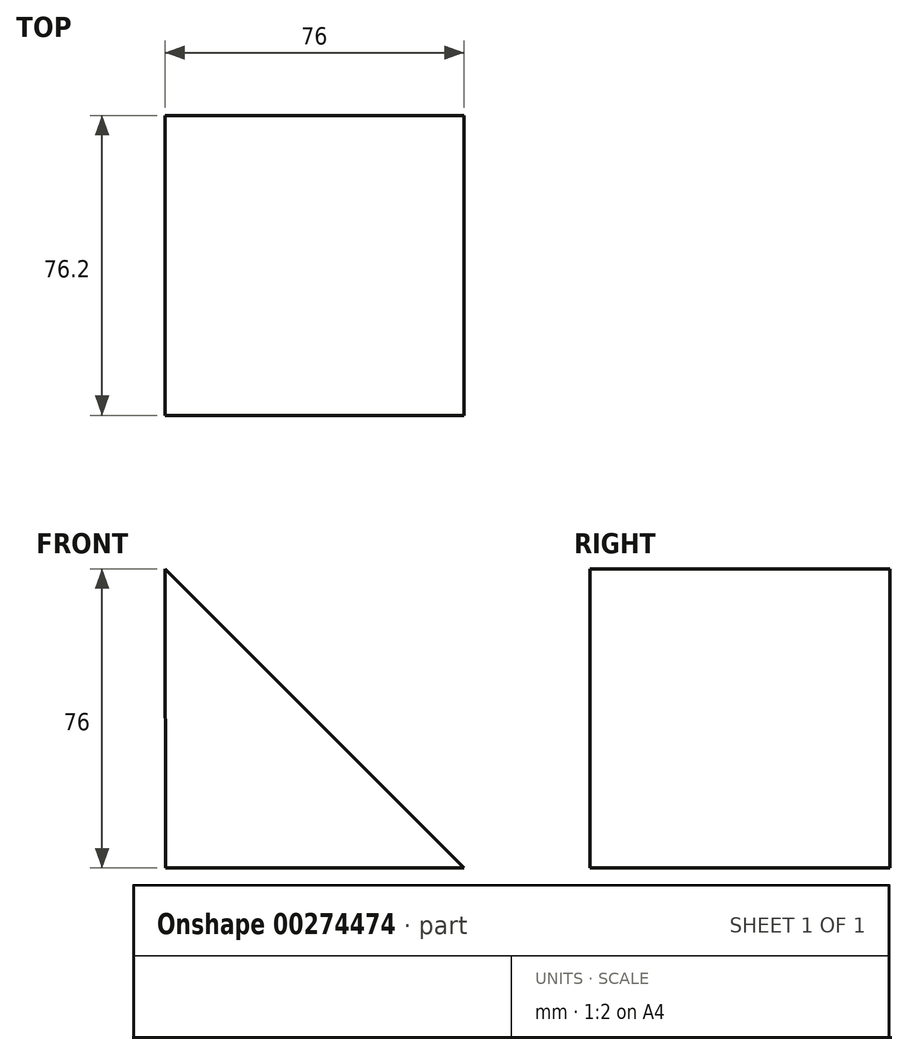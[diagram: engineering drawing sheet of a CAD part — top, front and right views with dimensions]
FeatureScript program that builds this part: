
annotation { "Feature Type Name" : "Feature", "Feature Type Description" : "" }
export const myFeature = defineFeature(function(context is Context, id is Id, definition is map)
    precondition{}
    {
        {
            var Q0;
            Q0=qCreatedBy(makeId("Front.planeOp"),FACE);
            var sketch = newSketch(context, id + "F0", { "sketchPlane" : qUnion([Q0])});
            skLineSegment(sketch, "E0", {"start": v(-76, 76) * mm, "end": v(0, 0) * mm});
            skLineSegment(sketch, "E1", {"start": v(0, 0) * mm, "end": v(-75.8, 0) * mm});
            skLineSegment(sketch, "E2", {"start": v(-75.8, 0) * mm, "end": v(-76, 76) * mm});
            skSolve(sketch);
        }
        {
            var Q0;
            Q0=makeQuery(id+"F0.imprint","IMPRINT",FACE,{"disambiguationData":[TD([[makeQuery(id+"F0.imprint","IMPRINT",EDGE,{"derivedFrom":sQuery(id+"F0.wireOp",EDGE,"E0")}),-1.0]])]});
            extrude(context, id + "F1", {"entities" : qUnion([Q0]), "depth" : 76.2 * mm});
        }
    });
